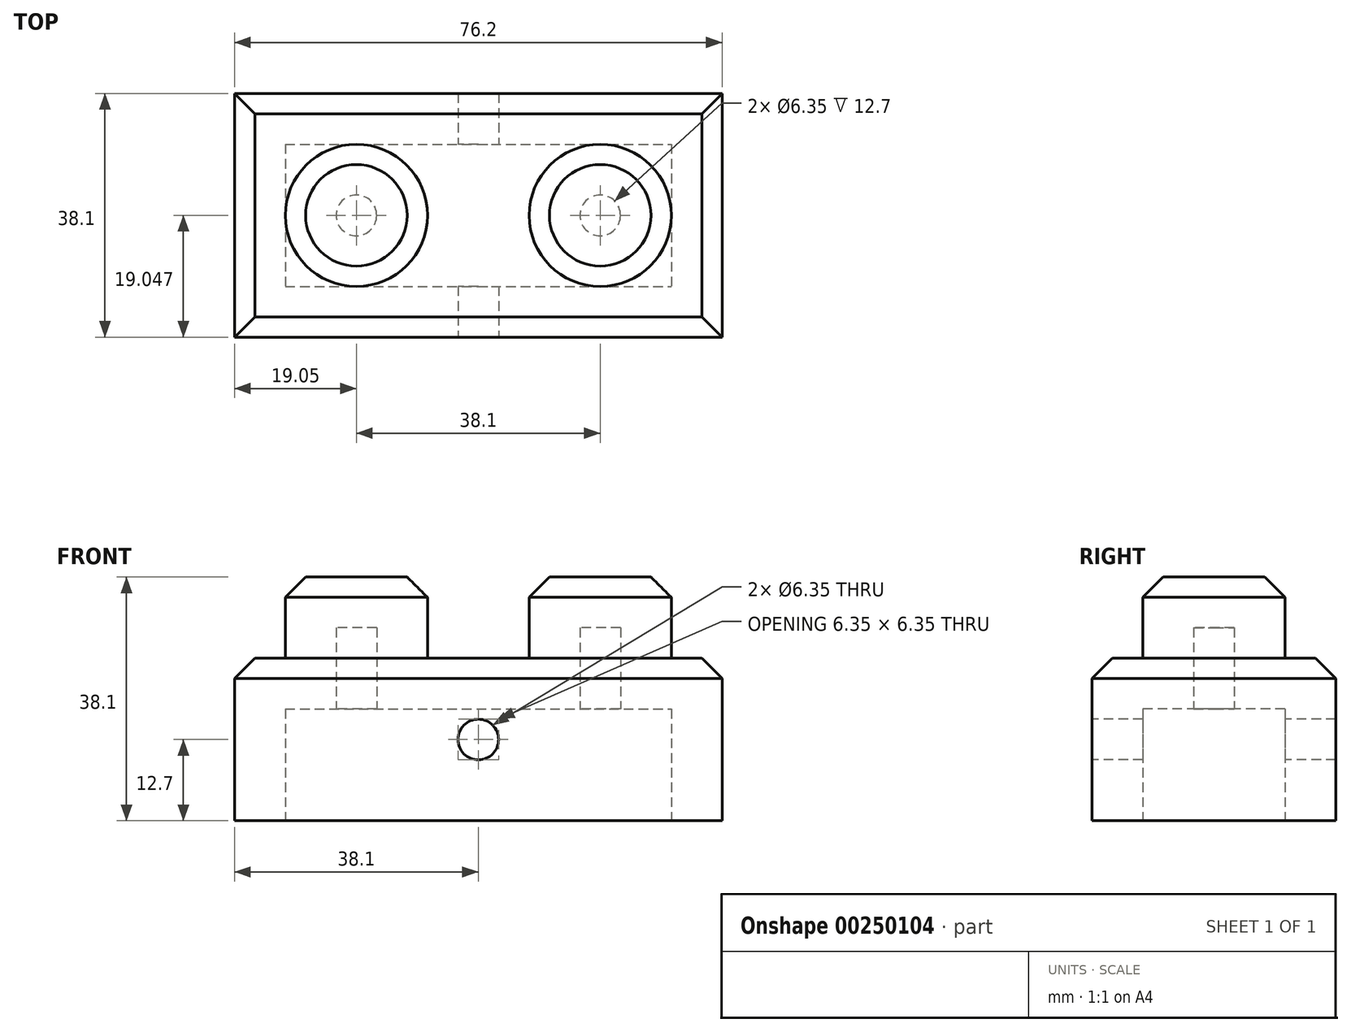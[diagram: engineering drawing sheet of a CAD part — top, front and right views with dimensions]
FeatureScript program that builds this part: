
annotation { "Feature Type Name" : "Feature", "Feature Type Description" : "" }
export const myFeature = defineFeature(function(context is Context, id is Id, definition is map)
    precondition{}
    {
        {
            var Q0;
            Q0=qCreatedBy(makeId("Top.planeOp"),FACE);
            var sketch = newSketch(context, id + "F0", { "sketchPlane" : qUnion([Q0])});
            skLineSegment(sketch, "E0.bottom", {"start": v(6.72, -4.68) * mm, "end": v(82.92, -4.68) * mm});
            skLineSegment(sketch, "E0.top", {"start": v(6.72, -42.78) * mm, "end": v(82.92, -42.78) * mm});
            skLineSegment(sketch, "E0.left", {"start": v(6.72, -4.68) * mm, "end": v(6.72, -42.78) * mm});
            skLineSegment(sketch, "E0.right", {"start": v(82.92, -4.68) * mm, "end": v(82.92, -42.78) * mm});
            skSolve(sketch);
        }
        {
            var Q0;
            Q0 = qSketchRegion(id + "F0", true);
            extrude(context, id + "F1", {"entities" : qUnion([Q0]), "depth" : 25.4 * mm});
        }
        {
            var Q0;
            Q0=makeQuery(id+"F1.opExtrude","CAP_FACE",FACE,{"disambiguationData":[OSD([sQuery(id+"F0.wireOp",EDGE,"E0.bottom"),sQuery(id+"F0.wireOp",EDGE,"E0.top"),sQuery(id+"F0.wireOp",EDGE,"E0.left"),sQuery(id+"F0.wireOp",EDGE,"E0.right")])],"isStart":false});
            var sketch = newSketch(context, id + "F2", { "sketchPlane" : qUnion([Q0])});
            skCircle(sketch, "E1", {"center": v(63.87, -23.73) * mm, "radius": 11.11 * mm});
            skCircle(sketch, "E2", {"center": v(25.77, -23.73) * mm, "radius": 11.11 * mm});
            skSolve(sketch);
        }
        {
            var Q0;
            Q0 = qSketchRegion(id + "F2", true);
            extrude(context, id + "F3", {"entities" : qUnion([Q0]), "operationType" : NewBodyOperationType.ADD, "depth" : 12.7 * mm});
        }
        {
            var Q0;
            Q0=makeQuery(id+"F1.opExtrude","CAP_FACE",FACE,{"disambiguationData":[OSD([sQuery(id+"F0.wireOp",EDGE,"E0.bottom"),sQuery(id+"F0.wireOp",EDGE,"E0.top"),sQuery(id+"F0.wireOp",EDGE,"E0.left"),sQuery(id+"F0.wireOp",EDGE,"E0.right")])],"isStart":true});
            shell(context, id + "F4", {"entities" : qUnion([Q0]), "thickness" : 7.94 * mm});
        }
        {
            var Q0;
            Q0=makeQuery(id+"F1.opExtrude","SWEPT_FACE",FACE,{"disambiguationData":[OSD([sQuery(id+"F0.wireOp",EDGE,"E0.top")])]});
            var sketch = newSketch(context, id + "F5", { "sketchPlane" : qUnion([Q0])});
            skCircle(sketch, "E3", {"center": v(44.82, 12.7) * mm, "radius": 3.18 * mm});
            skPoint(sketch, "E3.centerSnap0", {"position": v(82.92, 12.7) * mm});
            skPoint(sketch, "E3.centerSnap1", {"position": v(44.82, 25.4) * mm});
            skSolve(sketch);
        }
        {
            var Q0;
            Q0 = qSketchRegion(id + "F5", true);
            extrude(context, id + "F6", {"entities" : qUnion([Q0]), "operationType" : NewBodyOperationType.REMOVE, "oppositeDirection" : true, "depth" : 38.1 * mm});
        }
        {
            var Q0;
            Q0=makeQuery(id+"F3.opExtrude","CAP_FACE",FACE,{"disambiguationData":[OSD([sQuery(id+"F2.wireOp",EDGE,"E2")])],"isStart":false});
            var Q1;
            Q1=makeQuery(id+"F3.opExtrude","CAP_FACE",FACE,{"disambiguationData":[OSD([sQuery(id+"F2.wireOp",EDGE,"E1")])],"isStart":false});
            chamfer(context, id + "F7", {"entities" : qUnion([Q0, Q1]), "chamferType" : ChamferType.OFFSET_ANGLE, "width" : 3.17 * mm, "oppositeDirection" : false, "angle" : 45 * degree, "tangentPropagation" : true});
        }
        {
            var Q0;
            Q0=makeQuery(id+"F1.opExtrude","CAP_EDGE",EDGE,{"disambiguationData":[OSD([sQuery(id+"F0.wireOp",EDGE,"E0.bottom")])],"isStart":false});
            var Q1;
            Q1=makeQuery(id+"F1.opExtrude","CAP_EDGE",EDGE,{"disambiguationData":[OSD([sQuery(id+"F0.wireOp",EDGE,"E0.right")])],"isStart":false});
            var Q2;
            Q2=makeQuery(id+"F1.opExtrude","CAP_EDGE",EDGE,{"disambiguationData":[OSD([sQuery(id+"F0.wireOp",EDGE,"E0.top")])],"isStart":false});
            var Q3;
            Q3=makeQuery(id+"F1.opExtrude","CAP_EDGE",EDGE,{"disambiguationData":[OSD([sQuery(id+"F0.wireOp",EDGE,"E0.left")])],"isStart":false});
            chamfer(context, id + "F8", {"entities" : qUnion([Q0, Q1, Q2, Q3]), "chamferType" : ChamferType.OFFSET_ANGLE, "width" : 3.17 * mm, "oppositeDirection" : false, "angle" : 45 * degree, "tangentPropagation" : true});
        }
    });
